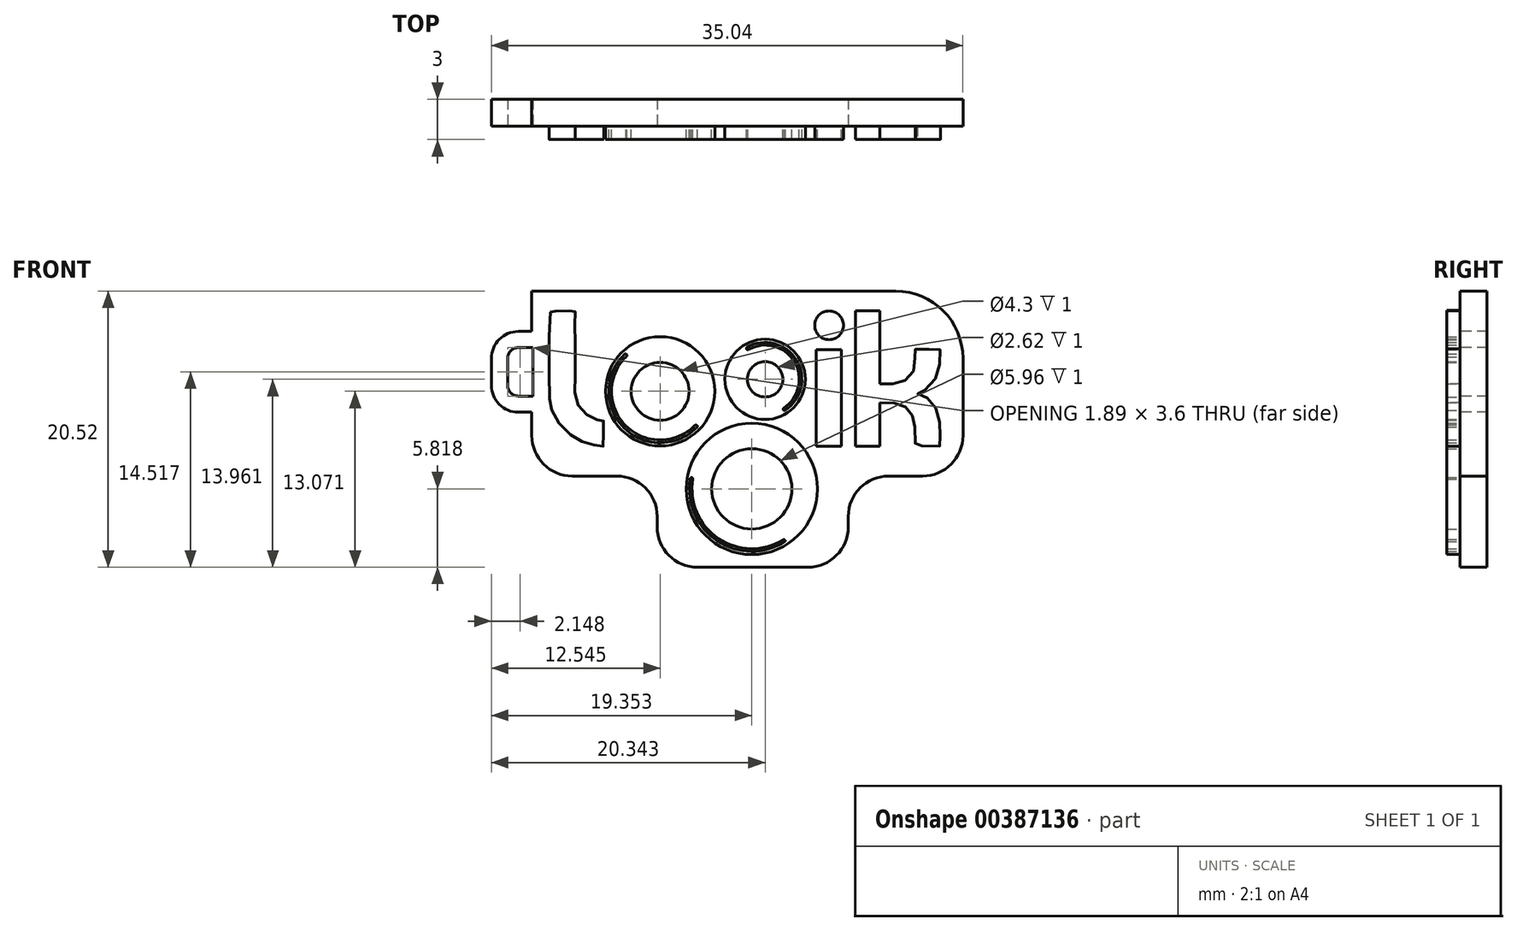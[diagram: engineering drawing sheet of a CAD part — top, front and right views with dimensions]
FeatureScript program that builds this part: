
annotation { "Feature Type Name" : "Feature", "Feature Type Description" : "" }
export const myFeature = defineFeature(function(context is Context, id is Id, definition is map)
    precondition{}
    {
        {
            var Q0;
            Q0=qCreatedBy(makeId("Front.planeOp"),FACE);
            var sketch = newSketch(context, id + "F0", { "sketchPlane" : qUnion([Q0])});
            skLineSegment(sketch, "E0.bottom", {"start": v(-15.42, 23.37) * mm, "end": v(29.52, 23.37) * mm});
            skLineSegment(sketch, "E0.top", {"start": v(-15.42, -6.63) * mm, "end": v(29.52, -6.63) * mm});
            skLineSegment(sketch, "E0.left", {"start": v(-15.42, 23.37) * mm, "end": v(-15.42, -6.63) * mm});
            skLineSegment(sketch, "E0.right", {"start": v(29.52, 23.37) * mm, "end": v(29.52, -6.63) * mm});
            skSolve(sketch);
        }
        {
            var Q0;
            Q0=makeQuery(id+"F0.imprint","IMPRINT",FACE,{"disambiguationData":[TD([[makeQuery(id+"F0.imprint","IMPRINT",EDGE,{"derivedFrom":sQuery(id+"F0.wireOp",EDGE,"E0.bottom")}),-1.0]])]});
            extrude(context, id + "F1", {"entities" : qUnion([Q0]), "depth" : 2 * mm});
        }
        {
            var Q0;
            Q0=makeQuery(id+"F1.opExtrude","CAP_FACE",FACE,{"disambiguationData":[OSD([sQuery(id+"F0.wireOp",EDGE,"E0.bottom"),sQuery(id+"F0.wireOp",EDGE,"E0.top"),sQuery(id+"F0.wireOp",EDGE,"E0.left"),sQuery(id+"F0.wireOp",EDGE,"E0.right")])],"isStart":false});
            var sketch = newSketch(context, id + "F2", { "sketchPlane" : qUnion([Q0])});
            skFitSpline(sketch, "E1", {"points": [v(-10.8, 18.04) * mm, v(-10.85, 12.14) * mm, v(-10.75, 10.95) * mm, v(-10.2, 9.83) * mm, v(-9.02, 8.73) * mm, v(-8.08, 8.3) * mm, v(-7.2, 8.08) * mm, v(-6.87, 8.06) * mm, v(-6.85, 9.05) * mm, v(-6.85, 10) * mm, v(-7.05, 10) * mm, v(-7.65, 10.14) * mm, v(-8.4, 10.71) * mm, v(-8.91, 11.56) * mm, v(-8.95, 13.19) * mm, v(-8.93, 15.03) * mm, v(-8.95, 16.57) * mm, v(-8.95, 18.05) * mm, v(-8.95, 18.14) * mm, v(-9.37, 18.14) * mm, v(-10.5, 18.1) * mm, v(-10.72, 18.15) * mm, v(-10.8, 18.04) * mm]});
            skCircle(sketch, "E2", {"center": v(-2.62, 12.14) * mm, "radius": 2.15 * mm});
            skCircle(sketch, "E3", {"center": v(-2.62, 12.14) * mm, "radius": 4.06 * mm});
            skArc(sketch, "E4", {"start": v(-5.28, 14.89) * mm, "mid": v(-5.32, 9.43) * mm, "end": v(0.14, 9.5) * mm});
            skArc(sketch, "E5", {"start": v(-5.17, 14.7) * mm, "mid": v(-5.18, 9.58) * mm, "end": v(-0.05, 9.6) * mm});
            skArc(sketch, "E6", {"start": v(-0.05, 9.6) * mm, "mid": v(0.08, 9.62) * mm, "end": v(0.14, 9.5) * mm});
            skArc(sketch, "E7", {"start": v(-5.28, 14.89) * mm, "mid": v(-5.11, 14.87) * mm, "end": v(-5.17, 14.7) * mm});
            skCircle(sketch, "E8", {"center": v(5.17, 13.03) * mm, "radius": 1.3 * mm});
            skCircle(sketch, "E9", {"center": v(5.17, 13.03) * mm, "radius": 2.99 * mm});
            skArc(sketch, "E10", {"start": v(3.89, 15.22) * mm, "mid": v(7.33, 14.36) * mm, "end": v(6.55, 10.9) * mm});
            skArc(sketch, "E11", {"start": v(3.83, 15.41) * mm, "mid": v(7.51, 14.44) * mm, "end": v(6.66, 10.74) * mm});
            skArc(sketch, "E12", {"start": v(3.83, 15.41) * mm, "mid": v(3.78, 15.3) * mm, "end": v(3.89, 15.22) * mm});
            skArc(sketch, "E13", {"start": v(6.55, 10.9) * mm, "mid": v(6.52, 10.77) * mm, "end": v(6.66, 10.74) * mm});
            skLineSegment(sketch, "E14.bottom", {"start": v(8.97, 15.22) * mm, "end": v(10.83, 15.22) * mm});
            skLineSegment(sketch, "E14.top", {"start": v(8.97, 8.06) * mm, "end": v(10.83, 8.06) * mm});
            skLineSegment(sketch, "E14.left", {"start": v(8.97, 15.22) * mm, "end": v(8.97, 8.06) * mm});
            skLineSegment(sketch, "E14.right", {"start": v(10.83, 15.22) * mm, "end": v(10.83, 8.06) * mm});
            skLineSegment(sketch, "E15.bottom", {"start": v(11.88, 18.12) * mm, "end": v(13.7, 18.12) * mm});
            skLineSegment(sketch, "E15.top", {"start": v(11.88, 8.06) * mm, "end": v(13.7, 8.06) * mm});
            skLineSegment(sketch, "E15.left", {"start": v(11.88, 18.12) * mm, "end": v(11.88, 8.06) * mm});
            skLineSegment(sketch, "E15.right", {"start": v(13.7, 18.12) * mm, "end": v(13.7, 12.7) * mm});
            skCircle(sketch, "E16", {"center": v(9.93, 17.04) * mm, "radius": 1.07 * mm});
            skFitSpline(sketch, "E17", {"points": [v(13.7, 12.7) * mm, v(14.32, 12.68) * mm, v(15.16, 12.76) * mm, v(15.7, 13.06) * mm, v(16.17, 13.62) * mm, v(16.3, 14.3) * mm, v(16.33, 15.04) * mm, v(16.35, 15.19) * mm, v(16.34, 15.28) * mm, v(16.51, 15.28) * mm, v(18.04, 15.28) * mm, v(18.17, 15.27) * mm, v(18.2, 15.12) * mm, v(18.13, 14.05) * mm, v(17.85, 13.15) * mm, v(17.2, 12.33) * mm, v(16.58, 11.99) * mm, v(16.48, 11.97) * mm, v(16.6, 11.92) * mm, v(17.04, 11.76) * mm, v(17.55, 11.34) * mm, v(17.99, 10.56) * mm, v(18.14, 9.72) * mm, v(18.16, 8.9) * mm, v(18.15, 8.14) * mm, v(18.16, 8.07) * mm, v(18.09, 8.07) * mm, v(16.42, 8.07) * mm, v(16.32, 8.07) * mm, v(16.32, 8.16) * mm, v(16.32, 9.2) * mm, v(16.23, 10) * mm, v(16.04, 10.47) * mm, v(15.75, 10.87) * mm, v(15.28, 11.16) * mm, v(14.65, 11.29) * mm, v(13.7, 11.3) * mm], "startDerivative": vector(19.55, -0.54) * mm, "endDerivative": vector(-26.93, -0.6) * mm});
            skLineSegment(sketch, "E18.trimOffspring", {"start": v(13.7, 11.3) * mm, "end": v(13.7, 8.06) * mm});
            skCircle(sketch, "E19", {"center": v(4.18, 4.89) * mm, "radius": 2.98 * mm});
            skCircle(sketch, "E20", {"center": v(4.18, 4.89) * mm, "radius": 4.88 * mm});
            skArc(sketch, "E21", {"start": v(-0.2, 5.62) * mm, "mid": v(1.7, 1.2) * mm, "end": v(6.52, 1.1) * mm});
            skArc(sketch, "E22", {"start": v(-0.4, 5.62) * mm, "mid": v(1.63, 1.02) * mm, "end": v(6.65, 0.96) * mm});
            skArc(sketch, "E23", {"start": v(-0.2, 5.62) * mm, "mid": v(-0.3, 5.73) * mm, "end": v(-0.4, 5.62) * mm});
            skArc(sketch, "E24", {"start": v(6.52, 1.1) * mm, "mid": v(6.64, 1.1) * mm, "end": v(6.65, 0.96) * mm});
            skSolve(sketch);
        }
        {
            var Q0;
            Q0=makeQuery(id+"F2.imprint","IMPRINT",FACE,{"disambiguationData":[TD([[makeQuery(id+"F2.imprint","IMPRINT",EDGE,{"derivedFrom":sQuery(id+"F2.wireOp",EDGE,"E14.bottom")}),-1.0]])]});
            var Q1;
            Q1=makeQuery(id+"F2.imprint","IMPRINT",FACE,{"disambiguationData":[TD([[makeQuery(id+"F2.imprint","IMPRINT",EDGE,{"derivedFrom":sQuery(id+"F2.wireOp",EDGE,"E15.bottom")}),-1.0]])]});
            var Q2;
            Q2=makeQuery(id+"F2.imprint","IMPRINT",FACE,{"disambiguationData":[TD([[makeQuery(id+"F2.imprint","IMPRINT",EDGE,{"derivedFrom":sQuery(id+"F2.wireOp",EDGE,"E16")}),1.0]])]});
            var Q3;
            Q3=makeQuery(id+"F2.imprint","IMPRINT",FACE,{"disambiguationData":[TD([[makeQuery(id+"F2.imprint","IMPRINT",EDGE,{"derivedFrom":sQuery(id+"F2.wireOp",EDGE,"E2")}),-1.0]])]});
            var Q4;
            Q4=makeQuery(id+"F2.imprint","IMPRINT",FACE,{"disambiguationData":[TD([[makeQuery(id+"F2.imprint","IMPRINT",EDGE,{"derivedFrom":sQuery(id+"F2.wireOp",EDGE,"E8")}),-1.0]])]});
            var Q5;
            Q5=makeQuery(id+"F2.imprint","IMPRINT",FACE,{"disambiguationData":[TD([[makeQuery(id+"F2.imprint","IMPRINT",EDGE,{"derivedFrom":sQuery(id+"F2.wireOp",EDGE,"E19")}),-1.0]])]});
            var Q6;
            Q6=makeQuery(id+"F2.imprint","IMPRINT",FACE,{"disambiguationData":[TD([[makeQuery(id+"F2.imprint","IMPRINT",EDGE,{"derivedFrom":sQuery(id+"F2.wireOp",EDGE,"E1")}),1.0]])]});
            extrude(context, id + "F3", {"entities" : qUnion([Q0, Q1, Q2, Q3, Q4, Q5, Q6]), "operationType" : NewBodyOperationType.ADD, "depth" : 1 * mm});
        }
        {
            var Q0;
            {var subQ0=sQuery(id+"F0.wireOp",EDGE,"E0.left");var subQ1=sQuery(id+"F0.wireOp",EDGE,"E0.bottom");var subQ2=sQuery(id+"F0.wireOp",EDGE,"E0.top");var subQ3=sQuery(id+"F0.wireOp",EDGE,"E0.right");Q0=makeQuery(id+"F3.boolean.opBoolean","SPLIT",FACE,{"disambiguationData":[TD([makeQuery(id+"F1.opExtrude","SWEPT_FACE",FACE,{"disambiguationData":[OSD([subQ1])]})])],"derivedFrom":makeQuery(id+"F1.opExtrude","CAP_FACE",FACE,{"disambiguationData":[OSD([subQ1,subQ2,subQ0,subQ3])],"isStart":false})});}
            var sketch = newSketch(context, id + "F4", { "sketchPlane" : qUnion([Q0])});
            skLineSegment(sketch, "E25.bottom", {"start": v(-12.17, 19.59) * mm, "end": v(14.87, 19.59) * mm});
            skLineSegment(sketch, "E25.top", {"start": v(0.15, -0.93) * mm, "end": v(8.35, -0.93) * mm});
            skLineSegment(sketch, "E25.left", {"start": v(-12.17, 19.59) * mm, "end": v(-12.17, 8.84) * mm});
            skLineSegment(sketch, "E25.right", {"start": v(19.87, 14.59) * mm, "end": v(19.87, 8.84) * mm});
            skPoint(sketch, "E26.visualSharp", {"position": v(19.87, 19.59) * mm});
            skArc(sketch, "E26.filletArc", {"start": v(19.87, 14.59) * mm, "mid": v(18.4, 18.12) * mm, "end": v(14.87, 19.59) * mm});
            skLineSegment(sketch, "E27", {"start": v(-9.17, 5.84) * mm, "end": v(-5.85, 5.84) * mm});
            skLineSegment(sketch, "E28", {"start": v(-2.85, 2.84) * mm, "end": v(-2.85, 2.07) * mm});
            skLineSegment(sketch, "E29", {"start": v(14.35, 5.84) * mm, "end": v(16.87, 5.84) * mm});
            skLineSegment(sketch, "E30", {"start": v(11.35, 2.84) * mm, "end": v(11.35, 2.07) * mm});
            skPoint(sketch, "E31.visualSharp", {"position": v(-2.85, 5.84) * mm});
            skArc(sketch, "E31.filletArc", {"start": v(-2.85, 2.84) * mm, "mid": v(-3.73, 4.96) * mm, "end": v(-5.85, 5.84) * mm});
            skPoint(sketch, "E32.visualSharp", {"position": v(11.35, 5.84) * mm});
            skArc(sketch, "E32.filletArc", {"start": v(14.35, 5.84) * mm, "mid": v(12.23, 4.96) * mm, "end": v(11.35, 2.84) * mm});
            skPoint(sketch, "E33.visualSharp", {"position": v(-12.17, 5.84) * mm});
            skArc(sketch, "E33.filletArc", {"start": v(-12.17, 8.84) * mm, "mid": v(-11.29, 6.72) * mm, "end": v(-9.17, 5.84) * mm});
            skPoint(sketch, "E34.visualSharp", {"position": v(19.87, 5.84) * mm});
            skArc(sketch, "E34.filletArc", {"start": v(16.87, 5.84) * mm, "mid": v(19, 6.72) * mm, "end": v(19.87, 8.84) * mm});
            skPoint(sketch, "E35.visualSharp", {"position": v(11.35, -0.93) * mm});
            skArc(sketch, "E35.filletArc", {"start": v(8.35, -0.93) * mm, "mid": v(10.47, -0.05) * mm, "end": v(11.35, 2.07) * mm});
            skPoint(sketch, "E36.visualSharp", {"position": v(-2.85, -0.93) * mm});
            skArc(sketch, "E36.filletArc", {"start": v(-2.85, 2.07) * mm, "mid": v(-1.97, -0.05) * mm, "end": v(0.15, -0.93) * mm});
            skLineSegment(sketch, "E37.bottom", {"start": v(-20.32, 25.87) * mm, "end": v(37.44, 25.87) * mm});
            skLineSegment(sketch, "E37.top", {"start": v(-20.32, -9.96) * mm, "end": v(37.44, -9.96) * mm});
            skLineSegment(sketch, "E37.left", {"start": v(-20.32, 25.87) * mm, "end": v(-20.32, -9.96) * mm});
            skLineSegment(sketch, "E37.right", {"start": v(37.44, 25.87) * mm, "end": v(37.44, -9.96) * mm});
            skSolve(sketch);
        }
        {
            var Q0;
            Q0 = qSketchRegion(id + "F4", true);
            extrude(context, id + "F5", {"entities" : qUnion([Q0]), "operationType" : NewBodyOperationType.REMOVE, "oppositeDirection" : true, "depth" : 25 * mm});
        }
        {
            var Q0;
            {var subQ0=sQuery(id+"F0.wireOp",EDGE,"E0.left");var subQ1=sQuery(id+"F0.wireOp",EDGE,"E0.bottom");var subQ2=sQuery(id+"F0.wireOp",EDGE,"E0.top");var subQ3=sQuery(id+"F0.wireOp",EDGE,"E0.right");Q0=makeQuery(id+"F3.boolean.opBoolean","SPLIT",FACE,{"disambiguationData":[TD([makeQuery(id+"F1.opExtrude","SWEPT_FACE",FACE,{"disambiguationData":[OSD([subQ1])]})])],"derivedFrom":makeQuery(id+"F1.opExtrude","CAP_FACE",FACE,{"disambiguationData":[OSD([subQ1,subQ2,subQ0,subQ3])],"isStart":false})});}
            var sketch = newSketch(context, id + "F6", { "sketchPlane" : qUnion([Q0])});
            skLineSegment(sketch, "E38", {"start": v(-12.17, 16.59) * mm, "end": v(-13.17, 16.59) * mm});
            skLineSegment(sketch, "E39", {"start": v(-15.17, 14.59) * mm, "end": v(-15.17, 12.59) * mm});
            skLineSegment(sketch, "E40", {"start": v(-13.17, 10.59) * mm, "end": v(-12.17, 10.59) * mm});
            skLineSegment(sketch, "E41", {"start": v(-12.17, 16.59) * mm, "end": v(-12.17, 10.59) * mm});
            skPoint(sketch, "E42.visualSharp", {"position": v(-15.17, 16.59) * mm});
            skArc(sketch, "E42.filletArc", {"start": v(-13.17, 16.59) * mm, "mid": v(-14.58, 16) * mm, "end": v(-15.17, 14.59) * mm});
            skPoint(sketch, "E43.visualSharp", {"position": v(-15.17, 10.59) * mm});
            skArc(sketch, "E43.filletArc", {"start": v(-15.17, 12.59) * mm, "mid": v(-14.58, 11.17) * mm, "end": v(-13.17, 10.59) * mm});
            skSolve(sketch);
        }
        {
            var Q0;
            Q0=makeQuery(id+"F6.imprint","IMPRINT",FACE,{"disambiguationData":[TD([[makeQuery(id+"F6.imprint","IMPRINT",EDGE,{"derivedFrom":sQuery(id+"F6.wireOp",EDGE,"E38")}),1.0]])]});
            extrude(context, id + "F7", {"entities" : qUnion([Q0]), "operationType" : NewBodyOperationType.ADD, "oppositeDirection" : true, "depth" : 2 * mm});
        }
        {
            var Q0;
            {var subQ0=sQuery(id+"F0.wireOp",EDGE,"E0.left");var subQ1=sQuery(id+"F0.wireOp",EDGE,"E0.bottom");var subQ2=sQuery(id+"F0.wireOp",EDGE,"E0.top");var subQ3=sQuery(id+"F0.wireOp",EDGE,"E0.right");Q0=makeQuery(id+"F7.boolean.opBoolean","MERGE",FACE,{"derivedFrom":[makeQuery(id+"F3.boolean.opBoolean","SPLIT",FACE,{"disambiguationData":[TD([makeQuery(id+"F1.opExtrude","SWEPT_FACE",FACE,{"disambiguationData":[OSD([subQ1])]})])],"derivedFrom":makeQuery(id+"F1.opExtrude","CAP_FACE",FACE,{"disambiguationData":[OSD([subQ1,subQ2,subQ0,subQ3])],"isStart":false})}),makeQuery(id+"F7.opExtrude","CAP_FACE",FACE,{"disambiguationData":[OSD([sQuery(id+"F6.wireOp",EDGE,"E38"),sQuery(id+"F6.wireOp",EDGE,"E39"),sQuery(id+"F6.wireOp",EDGE,"E40"),sQuery(id+"F6.wireOp",EDGE,"E41"),sQuery(id+"F6.wireOp",EDGE,"E42.filletArc"),sQuery(id+"F6.wireOp",EDGE,"E43.filletArc")])],"isStart":true})]});}
            var sketch = newSketch(context, id + "F8", { "sketchPlane" : qUnion([Q0])});
            skLineSegment(sketch, "E44.0", {"start": v(-12.17, 21.59) * mm, "end": v(-13.17, 21.59) * mm});
            skLineSegment(sketch, "E45.0", {"start": v(-13.17, 11.79) * mm, "end": v(-12.08, 11.79) * mm});
            skArc(sketch, "E45.1", {"start": v(-13.97, 12.59) * mm, "mid": v(-13.73, 12.02) * mm, "end": v(-13.17, 11.79) * mm});
            skLineSegment(sketch, "E45.2", {"start": v(-13.97, 14.59) * mm, "end": v(-13.97, 12.59) * mm});
            skArc(sketch, "E45.3", {"start": v(-13.17, 15.39) * mm, "mid": v(-13.73, 15.15) * mm, "end": v(-13.97, 14.59) * mm});
            skLineSegment(sketch, "E46", {"start": v(-12.08, 15.39) * mm, "end": v(-12.08, 11.79) * mm});
            skLineSegment(sketch, "E47", {"start": v(-13.17, 15.39) * mm, "end": v(-12.08, 15.39) * mm});
            skSolve(sketch);
        }
        {
            var Q0;
            Q0 = qSketchRegion(id + "F8", true);
            extrude(context, id + "F9", {"entities" : qUnion([Q0]), "operationType" : NewBodyOperationType.REMOVE, "oppositeDirection" : true, "depth" : 25 * mm});
        }
    });
